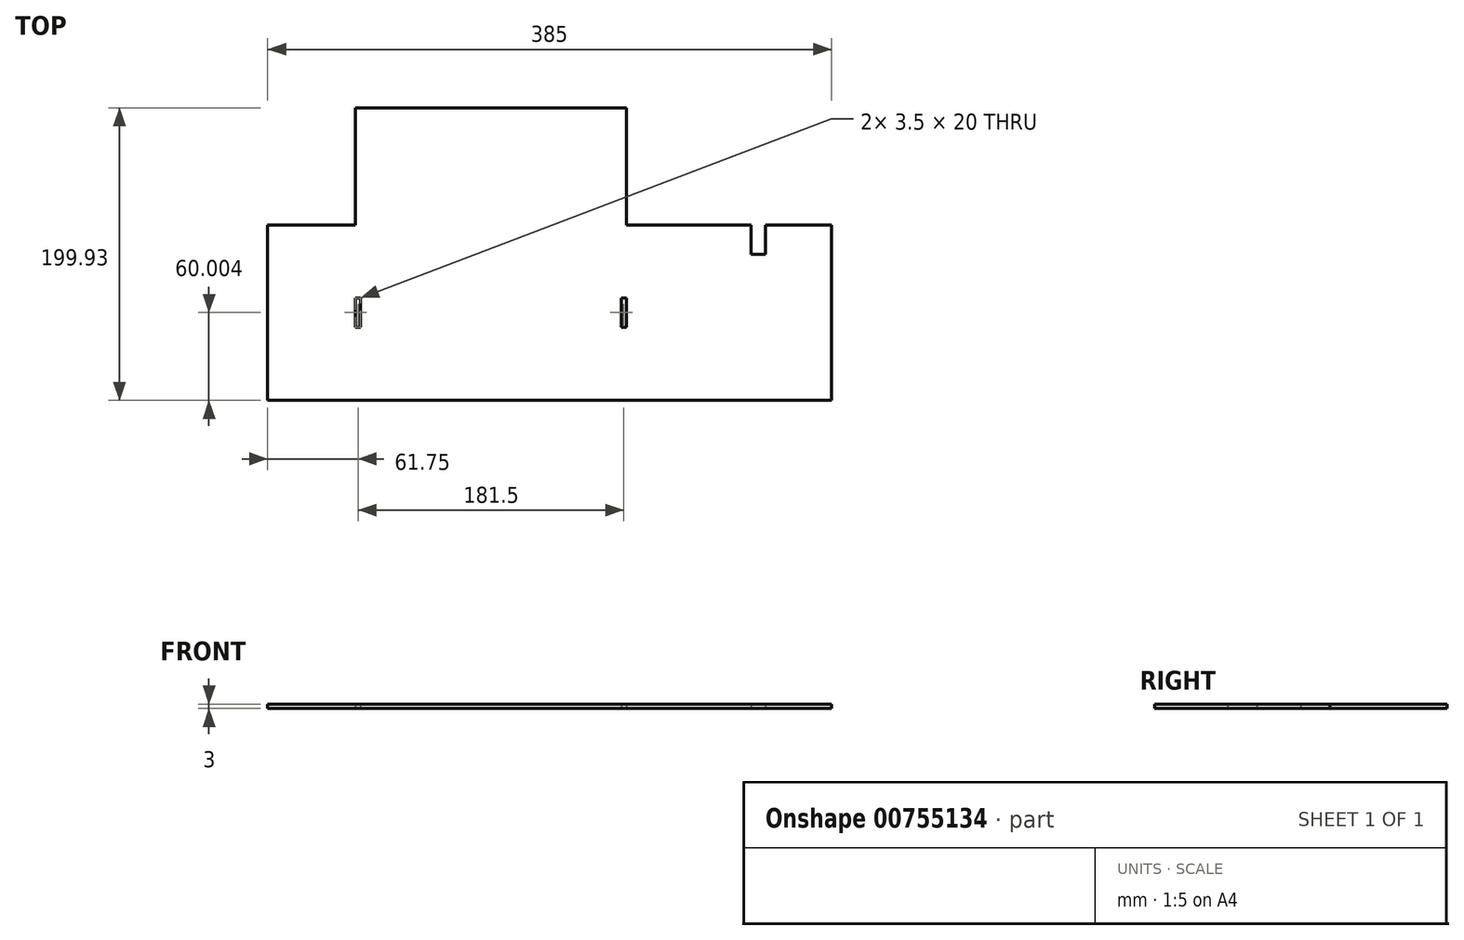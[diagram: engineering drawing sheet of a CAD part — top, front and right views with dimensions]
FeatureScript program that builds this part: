
annotation { "Feature Type Name" : "Feature", "Feature Type Description" : "" }
export const myFeature = defineFeature(function(context is Context, id is Id, definition is map)
    precondition{}
    {
        {
            var Q0;
            Q0=qCreatedBy(makeId("Top.planeOp"),FACE);
            var sketch = newSketch(context, id + "F0", { "sketchPlane" : qUnion([Q0])});
            skLineSegment(sketch, "E0", {"start": v(137.5, 20) * mm, "end": v(137.5, 0) * mm});
            skLineSegment(sketch, "E1", {"start": v(137.5, 20) * mm, "end": v(52.5, 20) * mm});
            skLineSegment(sketch, "E2", {"start": v(52.5, 100) * mm, "end": v(52.5, 20) * mm});
            skLineSegment(sketch, "E3", {"start": v(52.5, 100) * mm, "end": v(-132.5, 100) * mm});
            skLineSegment(sketch, "E4", {"start": v(-132.5, 100) * mm, "end": v(-132.5, 20) * mm});
            skLineSegment(sketch, "E5", {"start": v(-132.5, 20) * mm, "end": v(-192.5, 20) * mm});
            skLineSegment(sketch, "E6", {"start": v(-192.5, 20) * mm, "end": v(-192.5, -100) * mm});
            skLineSegment(sketch, "E7", {"start": v(192.5, -99.93) * mm, "end": v(-192.5, -99.93) * mm});
            skLineSegment(sketch, "E8", {"start": v(192.5, -100) * mm, "end": v(192.5, 20) * mm});
            skLineSegment(sketch, "E9", {"start": v(192.5, 20) * mm, "end": v(147.5, 20) * mm});
            skLineSegment(sketch, "E10", {"start": v(147.5, 20) * mm, "end": v(147.5, 0) * mm});
            skLineSegment(sketch, "E11", {"start": v(147.5, 0) * mm, "end": v(137.5, 0) * mm});
            skLineSegment(sketch, "E12.bottom", {"start": v(-132.5, -29.93) * mm, "end": v(-129, -29.93) * mm});
            skLineSegment(sketch, "E12.top", {"start": v(-132.5, -49.93) * mm, "end": v(-129, -49.93) * mm});
            skLineSegment(sketch, "E12.left", {"start": v(-132.5, -29.93) * mm, "end": v(-132.5, -49.93) * mm});
            skLineSegment(sketch, "E12.right", {"start": v(-129, -29.93) * mm, "end": v(-129, -49.93) * mm});
            skLineSegment(sketch, "E13.bottom", {"start": v(52.5, -29.93) * mm, "end": v(49, -29.93) * mm});
            skLineSegment(sketch, "E13.top", {"start": v(52.5, -49.93) * mm, "end": v(49, -49.93) * mm});
            skLineSegment(sketch, "E13.left", {"start": v(52.5, -29.93) * mm, "end": v(52.5, -49.93) * mm});
            skLineSegment(sketch, "E13.right", {"start": v(49, -29.93) * mm, "end": v(49, -49.93) * mm});
            skSolve(sketch);
        }
        {
            var Q0;
            Q0 = qSketchRegion(id + "F0", true);
            extrude(context, id + "F1", {"entities" : qUnion([Q0]), "depth" : 3 * mm, "offsetDistance" : 25 * mm});
        }
    });
